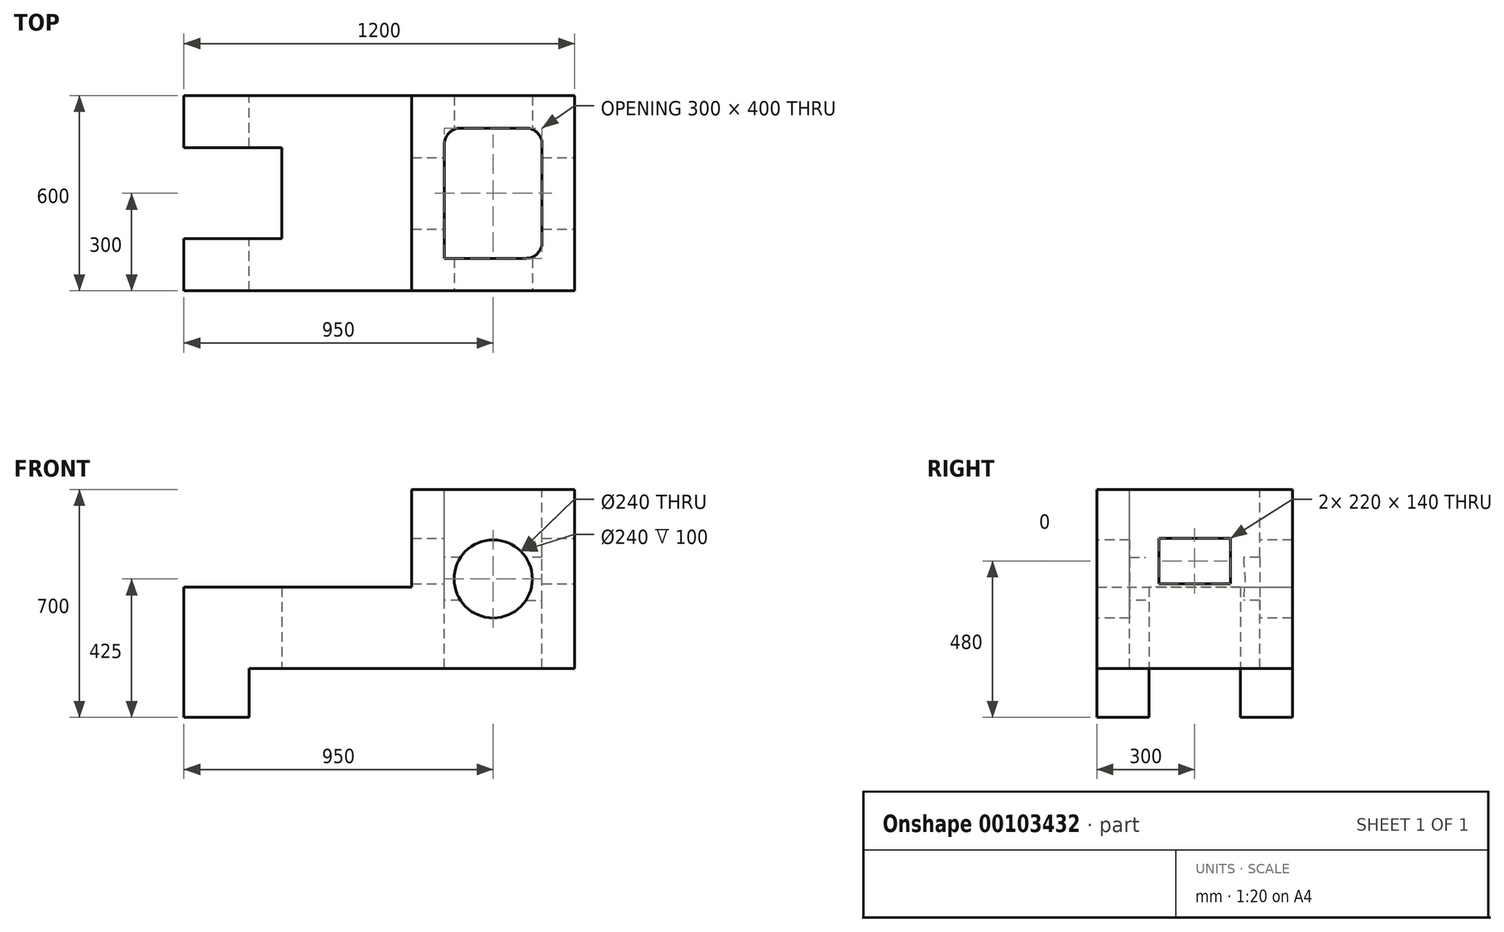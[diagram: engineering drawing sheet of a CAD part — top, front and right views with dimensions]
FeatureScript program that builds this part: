
annotation { "Feature Type Name" : "Feature", "Feature Type Description" : "" }
export const myFeature = defineFeature(function(context is Context, id is Id, definition is map)
    precondition{}
    {
        {
            var Q0;
            Q0=qCreatedBy(makeId("Front.planeOp"),FACE);
            var sketch = newSketch(context, id + "F0", { "sketchPlane" : qUnion([Q0])});
            skLineSegment(sketch, "E0.bottom", {"start": v(600, -125) * mm, "end": v(-400, -125) * mm});
            skLineSegment(sketch, "E0.top", {"start": v(100, 125) * mm, "end": v(-600, 125) * mm});
            skLineSegment(sketch, "E0.left", {"start": v(600, -125) * mm, "end": v(600, 125) * mm});
            skLineSegment(sketch, "E0.right", {"start": v(-600, -125) * mm, "end": v(-600, 125) * mm});
            skPoint(sketch, "E0.middle", {"position": v(0, 0) * mm});
            skLineSegment(sketch, "E1.top", {"start": v(600, 425) * mm, "end": v(100, 425) * mm});
            skLineSegment(sketch, "E1.left", {"start": v(600, 125) * mm, "end": v(600, 425) * mm});
            skLineSegment(sketch, "E1.right", {"start": v(100, 125) * mm, "end": v(100, 425) * mm});
            skLineSegment(sketch, "E2.top", {"start": v(-600, -275) * mm, "end": v(-400, -275) * mm});
            skLineSegment(sketch, "E2.left", {"start": v(-600, -125) * mm, "end": v(-600, -275) * mm});
            skLineSegment(sketch, "E2.right", {"start": v(-400, -125) * mm, "end": v(-400, -275) * mm});
            skSolve(sketch);
        }
        {
            var Q0;
            Q0=makeQuery(id+"F0.imprint","IMPRINT",FACE,{"disambiguationData":[TD([[makeQuery(id+"F0.imprint","IMPRINT",EDGE,{"derivedFrom":sQuery(id+"F0.wireOp",EDGE,"E0.bottom")}),-1.0]])]});
            extrude(context, id + "F1", {"entities" : qUnion([Q0]), "depth" : 600 * mm});
        }
        {
            var Q0;
            Q0=makeQuery(id+"F1.opExtrude","SWEPT_FACE",FACE,{"disambiguationData":[OSD([sQuery(id+"F0.wireOp",EDGE,"E0.top")])]});
            var sketch = newSketch(context, id + "F2", { "sketchPlane" : qUnion([Q0])});
            skLineSegment(sketch, "E3.bottom", {"start": v(-300, -160) * mm, "end": v(-600, -160) * mm});
            skLineSegment(sketch, "E3.top", {"start": v(-300, -440) * mm, "end": v(-600, -440) * mm});
            skLineSegment(sketch, "E3.left", {"start": v(-300, -160) * mm, "end": v(-300, -440) * mm});
            skPoint(sketch, "E3.middle", {"position": v(-600, -300) * mm});
            skLineSegment(sketch, "E4", {"start": v(-600, -160) * mm, "end": v(-600, -440) * mm});
            skPoint(sketch, "E3.right.start.orphan", {"position": v(-900, -160) * mm});
            skPoint(sketch, "E5.orphan", {"position": v(-900, -440) * mm});
            skSolve(sketch);
        }
        {
            var Q0;
            Q0=makeQuery(id+"F2.imprint","IMPRINT",FACE,{"disambiguationData":[TD([[makeQuery(id+"F2.imprint","IMPRINT",EDGE,{"derivedFrom":sQuery(id+"F2.wireOp",EDGE,"E3.bottom")}),1.0]])]});
            extrude(context, id + "F3", {"entities" : qUnion([Q0]), "operationType" : NewBodyOperationType.REMOVE, "endBound" : BoundingType.THROUGH_ALL, "depth" : 600 * mm, "hasSecondDirection" : true, "secondDirectionOppositeDirection" : true, "secondDirectionDepth" : 600 * mm});
        }
        {
            var Q0;
            Q0=makeQuery(id+"F1.opExtrude","CAP_FACE",FACE,{"disambiguationData":[OSD([sQuery(id+"F0.wireOp",EDGE,"E0.bottom"),sQuery(id+"F0.wireOp",EDGE,"E0.top"),sQuery(id+"F0.wireOp",EDGE,"E0.left"),sQuery(id+"F0.wireOp",EDGE,"E0.right"),sQuery(id+"F0.wireOp",EDGE,"E1.top"),sQuery(id+"F0.wireOp",EDGE,"E1.left"),sQuery(id+"F0.wireOp",EDGE,"E1.right"),sQuery(id+"F0.wireOp",EDGE,"E2.top"),sQuery(id+"F0.wireOp",EDGE,"E2.left"),sQuery(id+"F0.wireOp",EDGE,"E2.right")])],"isStart":false});
            var sketch = newSketch(context, id + "F4", { "sketchPlane" : qUnion([Q0])});
            skCircle(sketch, "E6", {"center": v(350, 150) * mm, "radius": 120 * mm});
            skPoint(sketch, "E6.centerSnap0", {"position": v(350, 425) * mm});
            skPoint(sketch, "E6.centerSnap1", {"position": v(600, 150) * mm});
            skSolve(sketch);
        }
        {
            var Q0;
            Q0=makeQuery(id+"F4.imprint","IMPRINT",FACE,{"disambiguationData":[TD([[makeQuery(id+"F4.imprint","IMPRINT",EDGE,{"derivedFrom":sQuery(id+"F4.wireOp",EDGE,"E6")}),1.0]])]});
            extrude(context, id + "F5", {"entities" : qUnion([Q0]), "operationType" : NewBodyOperationType.REMOVE, "oppositeDirection" : true, "depth" : 600 * mm});
        }
        {
            var Q0;
            Q0=makeQuery(id+"F1.opExtrude","SWEPT_FACE",FACE,{"disambiguationData":[OSD([sQuery(id+"F0.wireOp",EDGE,"E1.top")])]});
            var sketch = newSketch(context, id + "F6", { "sketchPlane" : qUnion([Q0])});
            skLineSegment(sketch, "E7.bottom", {"start": v(500, -500) * mm, "end": v(200, -500) * mm});
            skLineSegment(sketch, "E7.top", {"start": v(500, -100) * mm, "end": v(200, -100) * mm});
            skLineSegment(sketch, "E7.left", {"start": v(500, -500) * mm, "end": v(500, -100) * mm});
            skLineSegment(sketch, "E7.right", {"start": v(200, -500) * mm, "end": v(200, -100) * mm});
            skPoint(sketch, "E7.middle", {"position": v(350, -300) * mm});
            skPoint(sketch, "E7.middle.positionSnap0", {"position": v(350, -600) * mm});
            skPoint(sketch, "E7.middle.positionSnap1", {"position": v(100, -300) * mm});
            skPoint(sketch, "E7.centerSnap0", {"position": v(350, -600) * mm});
            skPoint(sketch, "E7.centerSnap1", {"position": v(100, -300) * mm});
            skSolve(sketch);
        }
        {
            var Q0;
            Q0=makeQuery(id+"F6.imprint","IMPRINT",FACE,{"disambiguationData":[TD([[makeQuery(id+"F6.imprint","IMPRINT",EDGE,{"derivedFrom":sQuery(id+"F6.wireOp",EDGE,"E7.bottom")}),-1.0]])]});
            extrude(context, id + "F7", {"entities" : qUnion([Q0]), "operationType" : NewBodyOperationType.REMOVE, "endBound" : BoundingType.THROUGH_ALL, "oppositeDirection" : true, "depth" : 25 * mm});
        }
        {
            var Q0;
            Q0=makeQuery(id+"F7.boolean.opBoolean","COPY",EDGE,{"derivedFrom":makeQuery(id+"F7.opExtrude","SWEPT_EDGE",EDGE,{"disambiguationData":[OSD([sQuery(id+"F6.wireOp",EDGE,"E7.top"),sQuery(id+"F6.wireOp",EDGE,"E7.right")])]})});
            fillet(context, id + "F8", {"entities" : qUnion([Q0]), "radius" : 50 * mm, "tangentPropagation" : true, "allowEdgeOverflow" : false});
        }
        {
            var Q0;
            Q0=makeQuery(id+"F7.boolean.opBoolean","COPY",EDGE,{"derivedFrom":makeQuery(id+"F7.opExtrude","SWEPT_EDGE",EDGE,{"disambiguationData":[OSD([sQuery(id+"F6.wireOp",EDGE,"E7.top"),sQuery(id+"F6.wireOp",EDGE,"E7.left")])]})});
            fillet(context, id + "F9", {"entities" : qUnion([Q0]), "radius" : 50 * mm, "tangentPropagation" : true, "allowEdgeOverflow" : false});
        }
        {
            var Q0;
            Q0=makeQuery(id+"F7.boolean.opBoolean","COPY",EDGE,{"derivedFrom":makeQuery(id+"F7.opExtrude","SWEPT_EDGE",EDGE,{"disambiguationData":[OSD([sQuery(id+"F6.wireOp",EDGE,"E7.bottom"),sQuery(id+"F6.wireOp",EDGE,"E7.left")])]})});
            fillet(context, id + "F10", {"entities" : qUnion([Q0]), "radius" : 50 * mm, "tangentPropagation" : true, "allowEdgeOverflow" : false});
        }
        {
            var Q0;
            Q0=makeQuery(id+"F1.opExtrude","SWEPT_FACE",FACE,{"disambiguationData":[OSD([sQuery(id+"F0.wireOp",EDGE,"E0.left"),sQuery(id+"F0.wireOp",EDGE,"E1.left")])]});
            var sketch = newSketch(context, id + "F11", { "sketchPlane" : qUnion([Q0])});
            skLineSegment(sketch, "E8.bottom", {"start": v(-410, 135) * mm, "end": v(-190, 135) * mm});
            skLineSegment(sketch, "E8.top", {"start": v(-410, 275) * mm, "end": v(-190, 275) * mm});
            skLineSegment(sketch, "E8.left", {"start": v(-410, 135) * mm, "end": v(-410, 275) * mm});
            skLineSegment(sketch, "E8.right", {"start": v(-190, 135) * mm, "end": v(-190, 275) * mm});
            skPoint(sketch, "E8.middle", {"position": v(-300, 205) * mm});
            skSolve(sketch);
        }
        {
            var Q0;
            Q0=makeQuery(id+"F11.imprint","IMPRINT",FACE,{"disambiguationData":[TD([[makeQuery(id+"F11.imprint","IMPRINT",EDGE,{"derivedFrom":sQuery(id+"F11.wireOp",EDGE,"E8.bottom")}),1.0]])]});
            extrude(context, id + "F12", {"entities" : qUnion([Q0]), "operationType" : NewBodyOperationType.REMOVE, "endBound" : BoundingType.THROUGH_ALL, "oppositeDirection" : true, "depth" : 25 * mm});
        }
    });
